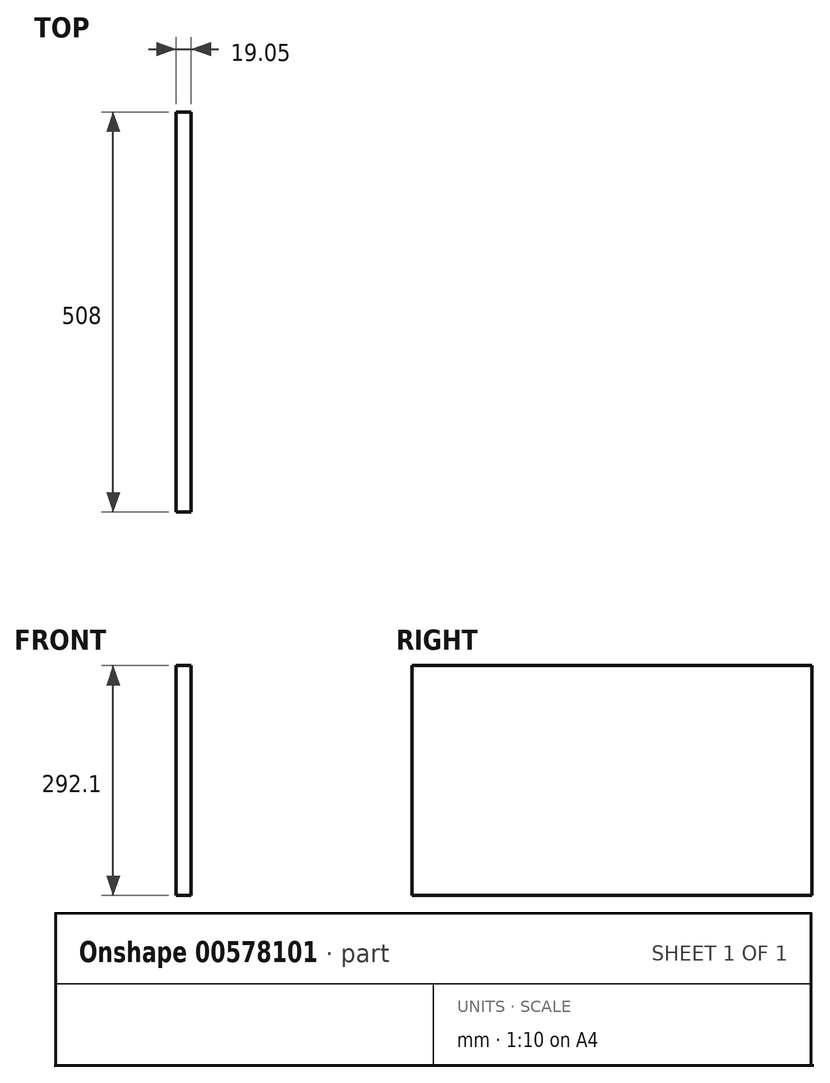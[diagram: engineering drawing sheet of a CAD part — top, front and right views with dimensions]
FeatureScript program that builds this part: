
annotation { "Feature Type Name" : "Feature", "Feature Type Description" : "" }
export const myFeature = defineFeature(function(context is Context, id is Id, definition is map)
    precondition{}
    {
        {
            var Q0;
            Q0=qCreatedBy(makeId("Right.planeOp"),FACE);
            var sketch = newSketch(context, id + "F0", { "sketchPlane" : qUnion([Q0])});
            skLineSegment(sketch, "E0.bottom", {"start": v(0, 0) * mm, "end": v(508, 0) * mm});
            skLineSegment(sketch, "E0.top", {"start": v(0, 292.1) * mm, "end": v(508, 292.1) * mm});
            skLineSegment(sketch, "E0.left", {"start": v(0, 0) * mm, "end": v(0, 292.1) * mm});
            skLineSegment(sketch, "E0.right", {"start": v(508, 0) * mm, "end": v(508, 292.1) * mm});
            skSolve(sketch);
        }
        {
            var Q0;
            Q0 = qSketchRegion(id + "F0", true);
            extrude(context, id + "F1", {"entities" : qUnion([Q0]), "depth" : 19.05 * mm, "offsetDistance" : 25.4 * mm});
        }
    });
